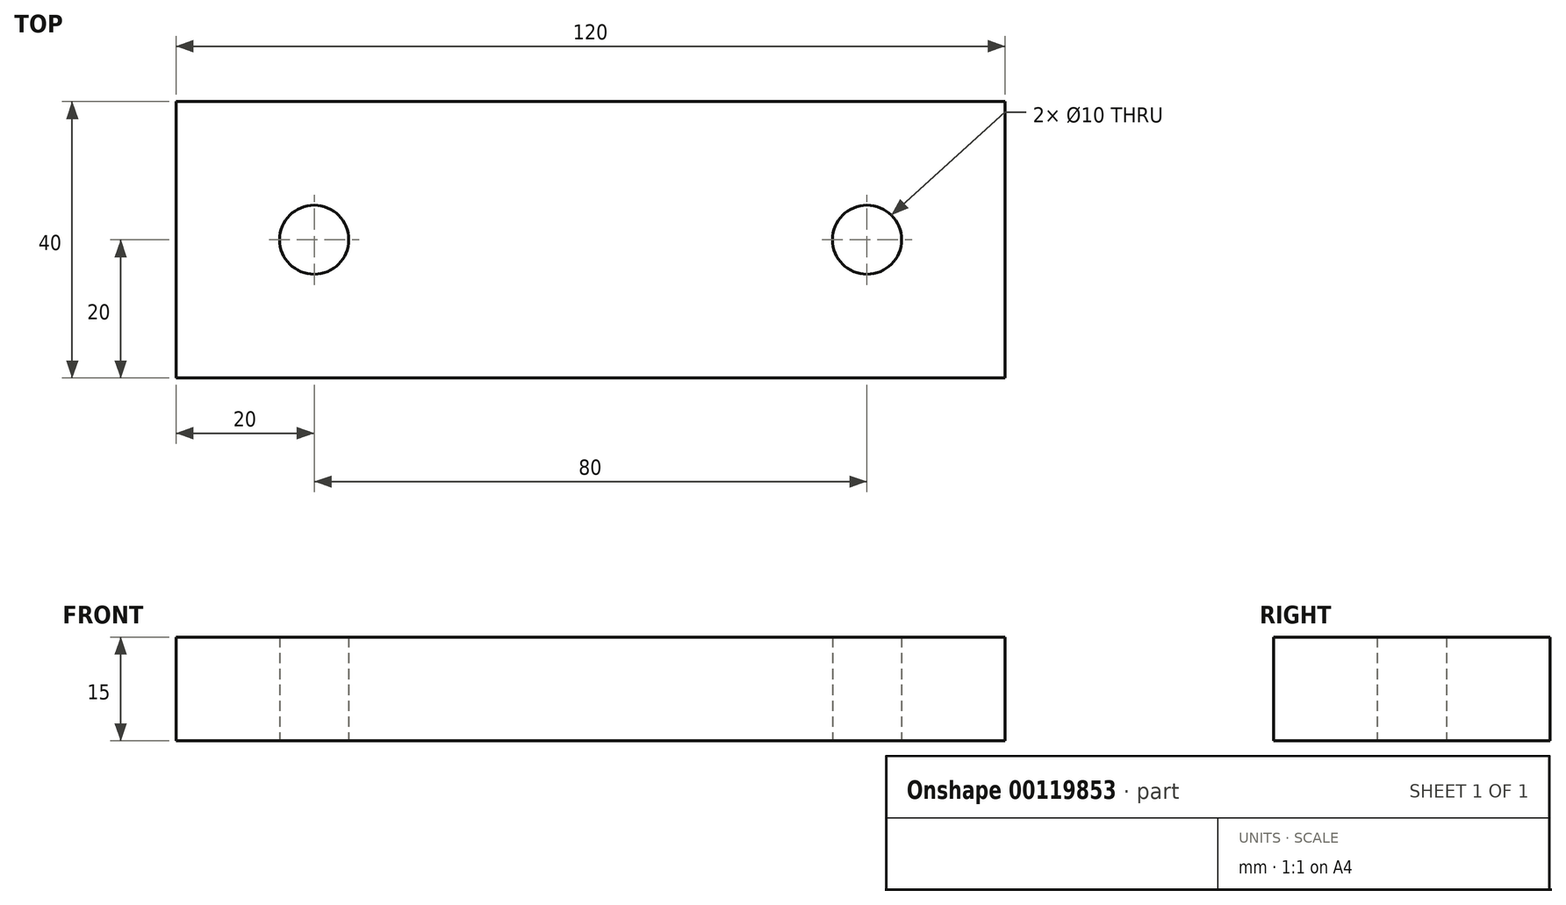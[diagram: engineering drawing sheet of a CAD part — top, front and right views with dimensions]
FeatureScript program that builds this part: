
annotation { "Feature Type Name" : "Feature", "Feature Type Description" : "" }
export const myFeature = defineFeature(function(context is Context, id is Id, definition is map)
    precondition{}
    {
        {
            var Q0;
            Q0=qCreatedBy(makeId("Top.planeOp"),FACE);
            var sketch = newSketch(context, id + "F0", { "sketchPlane" : qUnion([Q0])});
            skLineSegment(sketch, "E0.bottom", {"start": v(0, 0) * mm, "end": v(120, 0) * mm});
            skLineSegment(sketch, "E0.top", {"start": v(0, 40) * mm, "end": v(120, 40) * mm});
            skLineSegment(sketch, "E0.left", {"start": v(0, 0) * mm, "end": v(0, 40) * mm});
            skLineSegment(sketch, "E0.right", {"start": v(120, 0) * mm, "end": v(120, 40) * mm});
            skCircle(sketch, "E1", {"center": v(20, 20) * mm, "radius": 5 * mm});
            skCircle(sketch, "E2", {"center": v(100, 20) * mm, "radius": 5 * mm});
            skLineSegment(sketch, "E3", {"start": v(20, 40) * mm, "end": v(20, 0) * mm, "construction": true});
            skLineSegment(sketch, "E4", {"start": v(100, 40) * mm, "end": v(100, 0) * mm, "construction": true});
            skSolve(sketch);
        }
        {
            var Q0;
            Q0 = qSketchRegion(id + "F0", true);
            extrude(context, id + "F1", {"entities" : qUnion([Q0]), "depth" : 15 * mm});
        }
    });
